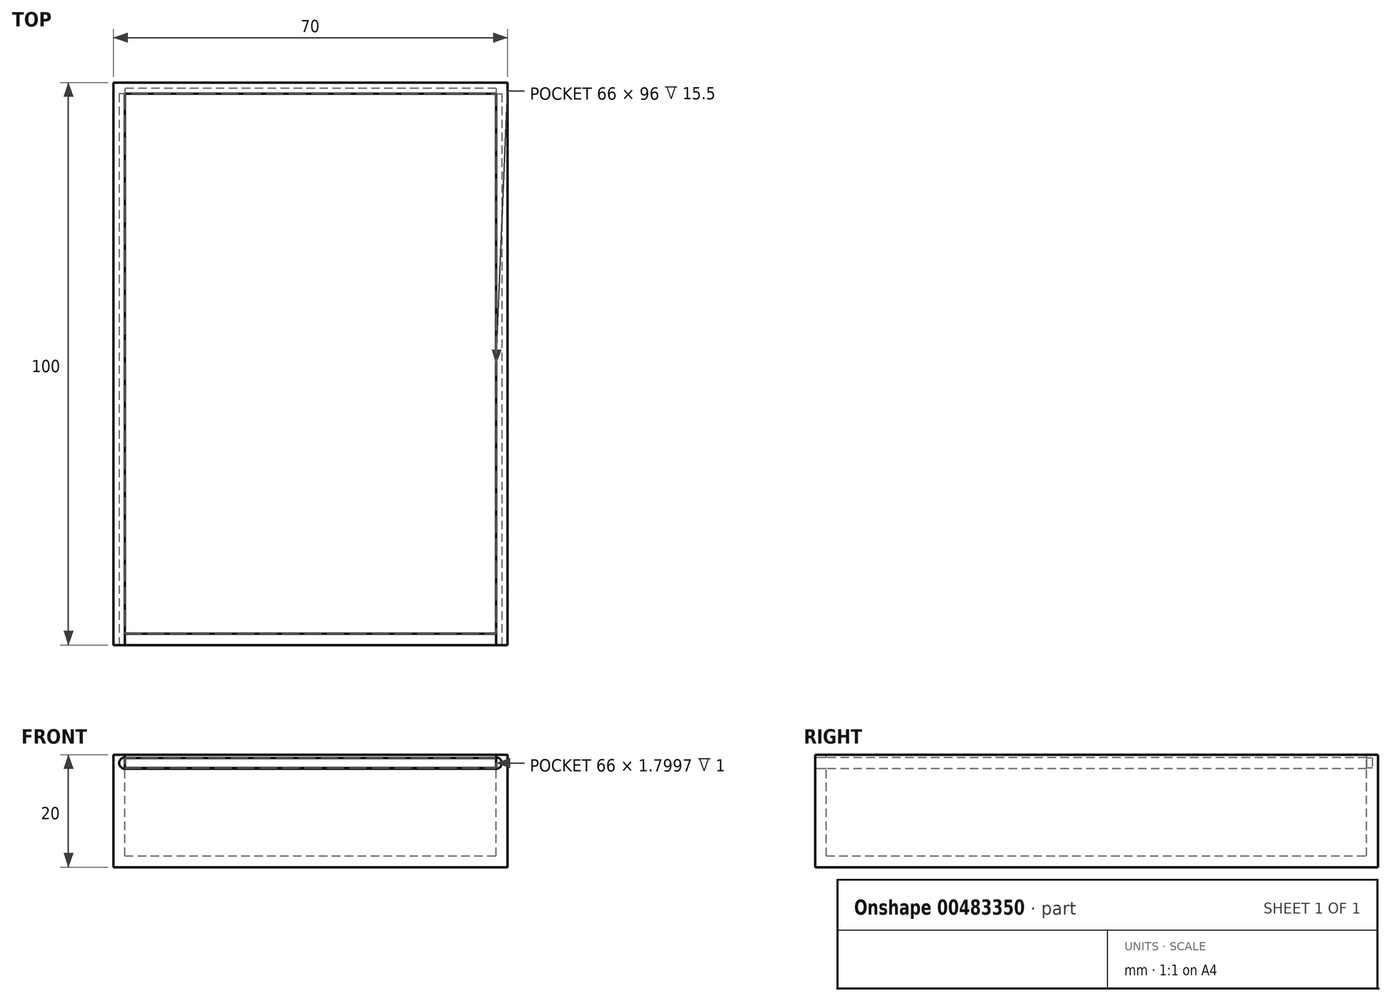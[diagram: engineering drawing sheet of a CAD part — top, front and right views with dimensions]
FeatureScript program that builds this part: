
annotation { "Feature Type Name" : "Feature", "Feature Type Description" : "" }
export const myFeature = defineFeature(function(context is Context, id is Id, definition is map)
    precondition{}
    {
        {
            var Q0;
            Q0=qCreatedBy(makeId("Top.planeOp"),FACE);
            var sketch = newSketch(context, id + "F0", { "sketchPlane" : qUnion([Q0])});
            skLineSegment(sketch, "E0.bottom", {"start": v(0, 0) * mm, "end": v(70, 0) * mm});
            skLineSegment(sketch, "E0.top", {"start": v(0, -100) * mm, "end": v(70, -100) * mm});
            skLineSegment(sketch, "E0.left", {"start": v(0, 0) * mm, "end": v(0, -100) * mm});
            skLineSegment(sketch, "E0.right", {"start": v(70, 0) * mm, "end": v(70, -100) * mm});
            skSolve(sketch);
        }
        {
            var Q0;
            Q0=makeQuery(id+"F0.imprint","IMPRINT",FACE,{"disambiguationData":[TD([[makeQuery(id+"F0.imprint","IMPRINT",EDGE,{"derivedFrom":sQuery(id+"F0.wireOp",EDGE,"E0.bottom")}),-1.0]])]});
            extrude(context, id + "F1", {"entities" : qUnion([Q0]), "depth" : 20 * mm});
        }
        {
            var Q0;
            Q0=makeQuery(id+"F1.opExtrude","CAP_FACE",FACE,{"disambiguationData":[OSD([sQuery(id+"F0.wireOp",EDGE,"E0.bottom"),sQuery(id+"F0.wireOp",EDGE,"E0.top"),sQuery(id+"F0.wireOp",EDGE,"E0.left"),sQuery(id+"F0.wireOp",EDGE,"E0.right")])],"isStart":false});
            var sketch = newSketch(context, id + "F2", { "sketchPlane" : qUnion([Q0])});
            skLineSegment(sketch, "E1.bottom", {"start": v(2, -98) * mm, "end": v(68, -98) * mm});
            skLineSegment(sketch, "E1.top", {"start": v(2, -2) * mm, "end": v(68, -2) * mm});
            skLineSegment(sketch, "E1.left", {"start": v(2, -98) * mm, "end": v(2, -2) * mm});
            skLineSegment(sketch, "E1.right", {"start": v(68, -98) * mm, "end": v(68, -2) * mm});
            skLineSegment(sketch, "E2", {"start": v(0, -50) * mm, "end": v(2, -50) * mm, "construction": true});
            skPoint(sketch, "E2.startSnap0", {"position": v(2, -50) * mm});
            skLineSegment(sketch, "E3", {"start": v(35, 0) * mm, "end": v(35, -2) * mm, "construction": true});
            skPoint(sketch, "E3.startSnap0", {"position": v(35, -2) * mm});
            skLineSegment(sketch, "E4", {"start": v(68, -50) * mm, "end": v(70, -50) * mm, "construction": true});
            skLineSegment(sketch, "E5", {"start": v(-11.06, -98) * mm, "end": v(-11.06, -100) * mm, "construction": true});
            skSolve(sketch);
        }
        {
            var Q0;
            Q0=makeQuery(id+"F2.imprint","IMPRINT",FACE,{"disambiguationData":[TD([[makeQuery(id+"F2.imprint","IMPRINT",EDGE,{"derivedFrom":sQuery(id+"F2.wireOp",EDGE,"E1.bottom")}),1.0]])]});
            extrude(context, id + "F3", {"entities" : qUnion([Q0]), "operationType" : NewBodyOperationType.REMOVE, "oppositeDirection" : true, "depth" : 18 * mm});
        }
        {
            var Q0;
            Q0=makeQuery(id+"F1.opExtrude","CAP_FACE",FACE,{"disambiguationData":[OSD([sQuery(id+"F0.wireOp",EDGE,"E0.bottom"),sQuery(id+"F0.wireOp",EDGE,"E0.top"),sQuery(id+"F0.wireOp",EDGE,"E0.left"),sQuery(id+"F0.wireOp",EDGE,"E0.right")])],"isStart":false});
            var sketch = newSketch(context, id + "F4", { "sketchPlane" : qUnion([Q0])});
            skLineSegment(sketch, "E6.bottom", {"start": v(2, -98) * mm, "end": v(67.99, -98) * mm});
            skLineSegment(sketch, "E6.top", {"start": v(2, -100) * mm, "end": v(67.99, -100) * mm});
            skLineSegment(sketch, "E6.left", {"start": v(2, -98) * mm, "end": v(2, -100) * mm});
            skLineSegment(sketch, "E6.right", {"start": v(67.99, -98) * mm, "end": v(67.99, -100) * mm});
            skSolve(sketch);
        }
        {
            var Q0;
            Q0 = qSketchRegion(id + "F4", true);
            extrude(context, id + "F5", {"entities" : qUnion([Q0]), "operationType" : NewBodyOperationType.REMOVE, "oppositeDirection" : true, "depth" : 2.5 * mm});
        }
        {
            var Q0;
            Q0=makeQuery(id+"F1.opExtrude","SWEPT_FACE",FACE,{"disambiguationData":[OSD([sQuery(id+"F0.wireOp",EDGE,"E0.top")])]});
            var sketch = newSketch(context, id + "F6", { "sketchPlane" : qUnion([Q0])});
            skPoint(sketch, "E7.first.point", {"position": v(67.99, 17.5) * mm});
            skCircle(sketch, "E8", {"center": v(2.01, 18.5) * mm, "radius": 1 * mm});
            skPoint(sketch, "E8.first.point", {"position": v(2, 17.5) * mm});
            skPoint(sketch, "E8.second.point", {"position": v(2, 19.5) * mm});
            skPoint(sketch, "E8.third.point", {"position": v(2.98, 18.75) * mm});
            skPoint(sketch, "E8.third.point.positionSnap0", {"position": v(2, 18.75) * mm});
            skCircle(sketch, "E9", {"center": v(68.02, 18.5) * mm, "radius": 1 * mm});
            skPoint(sketch, "E9.second.point", {"position": v(67.99, 19.5) * mm});
            skPoint(sketch, "E9.third.point", {"position": v(68.98, 18.75) * mm});
            skPoint(sketch, "E9.third.point.positionSnap0", {"position": v(67.99, 18.75) * mm});
            skSolve(sketch);
        }
        {
            var Q0;
            {var subQ0=sQuery(id+"F6.wireOp",EDGE,"E9");var subQ1=sQuery(id+"F4.wireOp",EDGE,"E6.top");var subQ2=makeQuery(id+"F5.boolean.opBoolean","COPY",EDGE,{"derivedFrom":makeQuery(id+"F5.opExtrude","SWEPT_EDGE",EDGE,{"disambiguationData":[OSD([sQuery(id+"F0.wireOp",EDGE,"E0.top"),subQ1,sQuery(id+"F4.wireOp",EDGE,"E6.right")])]})});var subQ4=makeQuery(id+"F6.imprint","INTERSECT",VERTEX,{"derivedFrom":[subQ2,subQ0]});Q0=makeQuery(id+"F6.imprint","IMPRINT",FACE,{"disambiguationData":[TD([[makeQuery(id+"F6.imprint","IMPRINT",EDGE,{"disambiguationData":[TD([[subQ4,1.0]])],"derivedFrom":subQ0}),1.0]])]});}
            var Q1;
            {var subQ0=sQuery(id+"F6.wireOp",EDGE,"E8");var subQ1=makeQuery(id+"F5.boolean.opBoolean","COPY",EDGE,{"derivedFrom":makeQuery(id+"F5.opExtrude","SWEPT_EDGE",EDGE,{"disambiguationData":[OSD([sQuery(id+"F0.wireOp",EDGE,"E0.top"),sQuery(id+"F4.wireOp",EDGE,"E6.top"),sQuery(id+"F4.wireOp",EDGE,"E6.left")])]})});var subQ2=makeQuery(id+"F6.imprint","INTERSECT",VERTEX,{"disambiguationData":[OD(0.0)],"derivedFrom":[subQ1,subQ0]});Q1=makeQuery(id+"F6.imprint","IMPRINT",FACE,{"disambiguationData":[TD([[makeQuery(id+"F6.imprint","IMPRINT",EDGE,{"disambiguationData":[TD([[subQ2,1.0]])],"derivedFrom":subQ0}),1.0]])]});}
            extrude(context, id + "F7", {"entities" : qUnion([Q0, Q1]), "operationType" : NewBodyOperationType.REMOVE, "oppositeDirection" : true, "depth" : 98 * mm});
        }
        {
            var Q0;
            {var subQ0=sQuery(id+"F4.wireOp",EDGE,"E6.top");var subQ1=sQuery(id+"F0.wireOp",EDGE,"E0.top");Q0=makeQuery(id+"F7.boolean.opBoolean","MERGE",FACE,{"derivedFrom":[makeQuery(id+"F3.boolean.opBoolean","COPY",FACE,{"derivedFrom":makeQuery(id+"F3.opExtrude","SWEPT_FACE",FACE,{"disambiguationData":[OSD([sQuery(id+"F2.wireOp",EDGE,"E1.top")])]})}),makeQuery(id+"F7.opExtrude","CAP_FACE",FACE,{"disambiguationData":[OSD([subQ1,subQ0,sQuery(id+"F4.wireOp",EDGE,"E6.left"),sQuery(id+"F6.wireOp",EDGE,"E8")])],"isStart":false}),makeQuery(id+"F7.opExtrude","CAP_FACE",FACE,{"disambiguationData":[OSD([subQ1,subQ0,sQuery(id+"F4.wireOp",EDGE,"E6.right"),sQuery(id+"F6.wireOp",EDGE,"E9")])],"isStart":false})]});}
            var sketch = newSketch(context, id + "F8", { "sketchPlane" : qUnion([Q0])});
            skLineSegment(sketch, "E10", {"start": v(68, 19.5) * mm, "end": v(68, 19.4) * mm, "construction": true});
            skLineSegment(sketch, "E11", {"start": v(68, 17.5) * mm, "end": v(68, 17.6) * mm, "construction": true});
            skLineSegment(sketch, "E12.bottom", {"start": v(68, 19.4) * mm, "end": v(2, 19.4) * mm});
            skLineSegment(sketch, "E12.top", {"start": v(68, 17.6) * mm, "end": v(2, 17.6) * mm});
            skLineSegment(sketch, "E12.left", {"start": v(68, 19.4) * mm, "end": v(68, 17.6) * mm});
            skLineSegment(sketch, "E12.right", {"start": v(2, 19.4) * mm, "end": v(2, 17.6) * mm});
            skLineSegment(sketch, "E13", {"start": v(2, 19.5) * mm, "end": v(2, 19.4) * mm, "construction": true});
            skSolve(sketch);
        }
        {
            var Q0;
            Q0=makeQuery(id+"F8.imprint","IMPRINT",FACE,{"disambiguationData":[TD([[makeQuery(id+"F8.imprint","IMPRINT",EDGE,{"derivedFrom":sQuery(id+"F8.wireOp",EDGE,"E12.bottom")}),1.0]])]});
            extrude(context, id + "F9", {"entities" : qUnion([Q0]), "operationType" : NewBodyOperationType.REMOVE, "oppositeDirection" : true, "depth" : 1 * mm});
        }
    });
